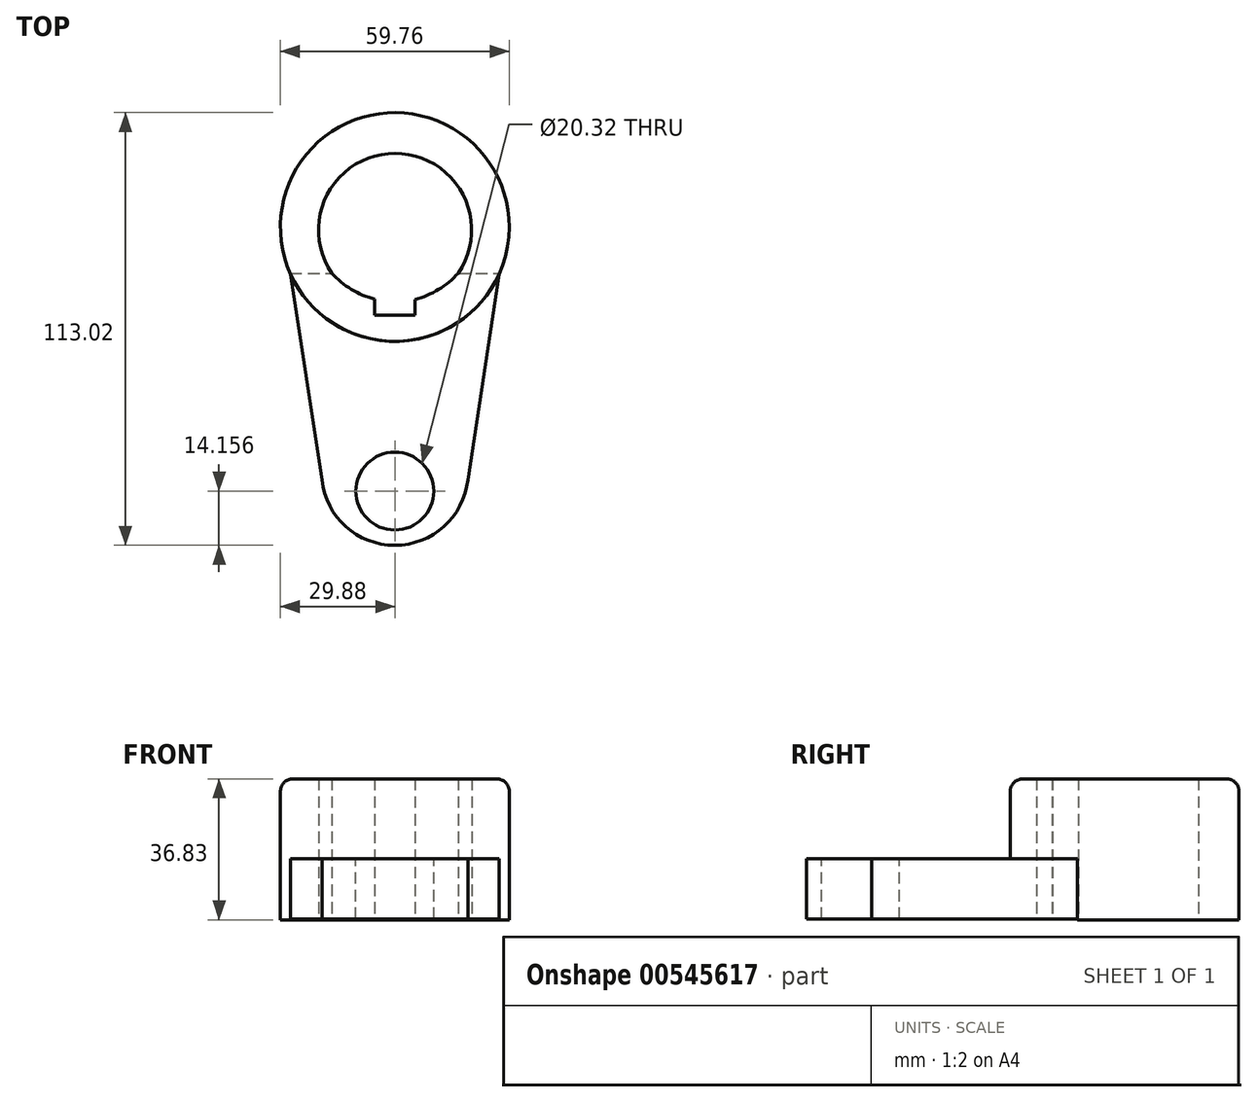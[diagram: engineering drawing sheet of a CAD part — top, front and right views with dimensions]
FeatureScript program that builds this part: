
annotation { "Feature Type Name" : "Feature", "Feature Type Description" : "" }
export const myFeature = defineFeature(function(context is Context, id is Id, definition is map)
    precondition{}
    {
        {
            var Q0;
            Q0=qCreatedBy(makeId("Top.planeOp"),FACE);
            var sketch = newSketch(context, id + "F0", { "sketchPlane" : qUnion([Q0])});
            skLineSegment(sketch, "E0", {"start": v(-27.26, -32.57) * mm, "end": v(27.26, -32.57) * mm});
            skArc(sketch, "E1", {"start": v(-19.05, -86.55) * mm, "mid": v(0, -103.67) * mm, "end": v(19.05, -86.55) * mm});
            skLineSegment(sketch, "E2", {"start": v(-27.26, -32.57) * mm, "end": v(-19.05, -86.55) * mm});
            skLineSegment(sketch, "E3", {"start": v(27.26, -32.57) * mm, "end": v(19.05, -86.55) * mm});
            skSolve(sketch);
        }
        {
            var Q0;
            Q0=makeQuery(id+"F0.imprint","IMPRINT",FACE,{"disambiguationData":[TD([[makeQuery(id+"F0.imprint","IMPRINT",EDGE,{"derivedFrom":sQuery(id+"F0.wireOp",EDGE,"E0")}),-1.0]])]});
            extrude(context, id + "F1", {"entities" : qUnion([Q0]), "depth" : 15.77 * mm, "offsetDistance" : 25.4 * mm});
        }
        {
            var Q0;
            Q0=makeQuery(id+"F1.opExtrude","CAP_FACE",FACE,{"disambiguationData":[OSD([sQuery(id+"F0.wireOp",EDGE,"E0"),sQuery(id+"F0.wireOp",EDGE,"E1"),sQuery(id+"F0.wireOp",EDGE,"E2"),sQuery(id+"F0.wireOp",EDGE,"E3")])],"isStart":false});
            var sketch = newSketch(context, id + "F2", { "sketchPlane" : qUnion([Q0])});
            skCircle(sketch, "E4", {"center": v(0, -89.51) * mm, "radius": 10.16 * mm});
            skSolve(sketch);
        }
        {
            var Q0;
            Q0=sQuery(id+"F2.wireOp",VERTEX,"E4.center");
            var Q1;
            Q1=makeQuery(id+"F1.opExtrude","SWEPT_BODY",BODY,{"disambiguationData":[OSD([sQuery(id+"F0.wireOp",EDGE,"E0"),sQuery(id+"F0.wireOp",EDGE,"E1"),sQuery(id+"F0.wireOp",EDGE,"E2"),sQuery(id+"F0.wireOp",EDGE,"E3")])]});
            hole(context, id + "F3", {"style" : HoleStyle.SIMPLE, "endStyle" : HoleEndStyle.THROUGH, "holeDiameter" : 20.32 * mm, "majorDiameter" : 6.35 * mm, "isTappedThrough" : true, "tappedDepth" : 12.7 * mm, "tapClearance" : 3, "locations" : qUnion([Q0]), "scope" : qUnion([Q1])});
        }
        {
            var Q0;
            Q0=makeQuery(id+"F1.opExtrude","CAP_FACE",FACE,{"disambiguationData":[OSD([sQuery(id+"F0.wireOp",EDGE,"E0"),sQuery(id+"F0.wireOp",EDGE,"E1"),sQuery(id+"F0.wireOp",EDGE,"E2"),sQuery(id+"F0.wireOp",EDGE,"E3")])],"isStart":false});
            var sketch = newSketch(context, id + "F4", { "sketchPlane" : qUnion([Q0])});
            skCircle(sketch, "E5", {"center": v(0, -20.53) * mm, "radius": 29.88 * mm});
            skArc(sketch, "E6", {"start": v(9.1, -39.13) * mm, "mid": v(-0.11, -1.28) * mm, "end": v(-8.67, -39.28) * mm});
            skLineSegment(sketch, "E7.top", {"start": v(-8.67, -44.9) * mm, "end": v(9.25, -44.9) * mm});
            skLineSegment(sketch, "E7.left", {"start": v(-8.67, -39.28) * mm, "end": v(-8.67, -44.9) * mm});
            skLineSegment(sketch, "E7.right", {"start": v(9.25, -39.28) * mm, "end": v(9.25, -44.9) * mm});
            skSolve(sketch);
        }
        {
            var Q0;
            {var subQ0=makeQuery(id+"F1.opExtrude","CAP_EDGE",EDGE,{"disambiguationData":[OSD([sQuery(id+"F0.wireOp",EDGE,"E2")])],"isStart":false});var subQ8=sQuery(id+"F4.wireOp",EDGE,"E5");var subQ9=makeQuery(id+"F4.imprint","INTERSECT",VERTEX,{"derivedFrom":[subQ0,subQ8]});Q0=makeQuery(id+"F4.imprint","IMPRINT",FACE,{"disambiguationData":[TD([[makeQuery(id+"F4.imprint","IMPRINT",EDGE,{"disambiguationData":[TD([[subQ9,1.0]])],"derivedFrom":subQ8}),1.0]])]});}
            var Q1;
            {var subQ6=makeQuery(id+"F1.opExtrude","CAP_EDGE",EDGE,{"disambiguationData":[OSD([sQuery(id+"F0.wireOp",EDGE,"E2")])],"isStart":false});var subQ8=sQuery(id+"F4.wireOp",EDGE,"E5");var subQ9=makeQuery(id+"F4.imprint","INTERSECT",VERTEX,{"derivedFrom":[subQ6,subQ8]});Q1=makeQuery(id+"F4.imprint","IMPRINT",FACE,{"disambiguationData":[TD([[makeQuery(id+"F4.imprint","IMPRINT",EDGE,{"disambiguationData":[TD([[subQ9,-1.0]])],"derivedFrom":subQ8}),1.0]])]});}
            extrude(context, id + "F5", {"entities" : qUnion([Q0, Q1]), "operationType" : NewBodyOperationType.ADD, "depth" : 20.83 * mm, "offsetDistance" : 25.4 * mm});
        }
        {
            var Q0;
            Q0=makeQuery(id+"F5.opExtrude","CAP_FACE",FACE,{"disambiguationData":[OSD([sQuery(id+"F0.wireOp",EDGE,"E0"),sQuery(id+"F4.wireOp",EDGE,"E5"),sQuery(id+"F4.wireOp",EDGE,"E6")])],"isStart":true});
            extrude(context, id + "F6", {"entities" : qUnion([Q0]), "operationType" : NewBodyOperationType.ADD, "depth" : 16 * mm, "offsetDistance" : 25.4 * mm});
        }
        {
            var Q0;
            Q0=makeQuery(id+"F1.opExtrude","CAP_FACE",FACE,{"disambiguationData":[OSD([sQuery(id+"F0.wireOp",EDGE,"E0"),sQuery(id+"F0.wireOp",EDGE,"E1"),sQuery(id+"F0.wireOp",EDGE,"E2"),sQuery(id+"F0.wireOp",EDGE,"E3")])],"isStart":true});
            var sketch = newSketch(context, id + "F7", { "sketchPlane" : qUnion([Q0])});
            skArc(sketch, "E8", {"start": v(-5.24, 39.4) * mm, "mid": v(-11.35, 36.81) * mm, "end": v(-16.45, 32.57) * mm});
            skArc(sketch, "E9", {"start": v(16.57, 32.57) * mm, "mid": v(11.43, 36.85) * mm, "end": v(5.25, 39.43) * mm});
            skLineSegment(sketch, "E10.top", {"start": v(-5.24, 43.55) * mm, "end": v(5.25, 43.55) * mm});
            skLineSegment(sketch, "E10.left", {"start": v(-5.24, 39.4) * mm, "end": v(-5.24, 43.55) * mm});
            skLineSegment(sketch, "E10.right", {"start": v(5.25, 39.4) * mm, "end": v(5.25, 43.55) * mm});
            skSolve(sketch);
        }
        {
            var Q0;
            Q0=makeQuery(id+"F5.opExtrude","CAP_EDGE",EDGE,{"disambiguationData":[OSD([sQuery(id+"F4.wireOp",EDGE,"E5")])],"isStart":false});
            fillet(context, id + "F8", {"entities" : qUnion([Q0]), "radius" : 3.3 * mm, "tangentPropagation" : true, "allowEdgeOverflow" : false});
        }
        {
            var Q0;
            Q0=makeQuery(id+"F7.imprint","IMPRINT",FACE,{"disambiguationData":[TD([[makeQuery(id+"F7.imprint","IMPRINT",EDGE,{"derivedFrom":sQuery(id+"F7.wireOp",EDGE,"E8")}),1.0]])]});
            extrude(context, id + "F9", {"entities" : qUnion([Q0]), "operationType" : NewBodyOperationType.REMOVE, "oppositeDirection" : true, "depth" : 39.37 * mm, "offsetDistance" : 25.4 * mm});
        }
    });
